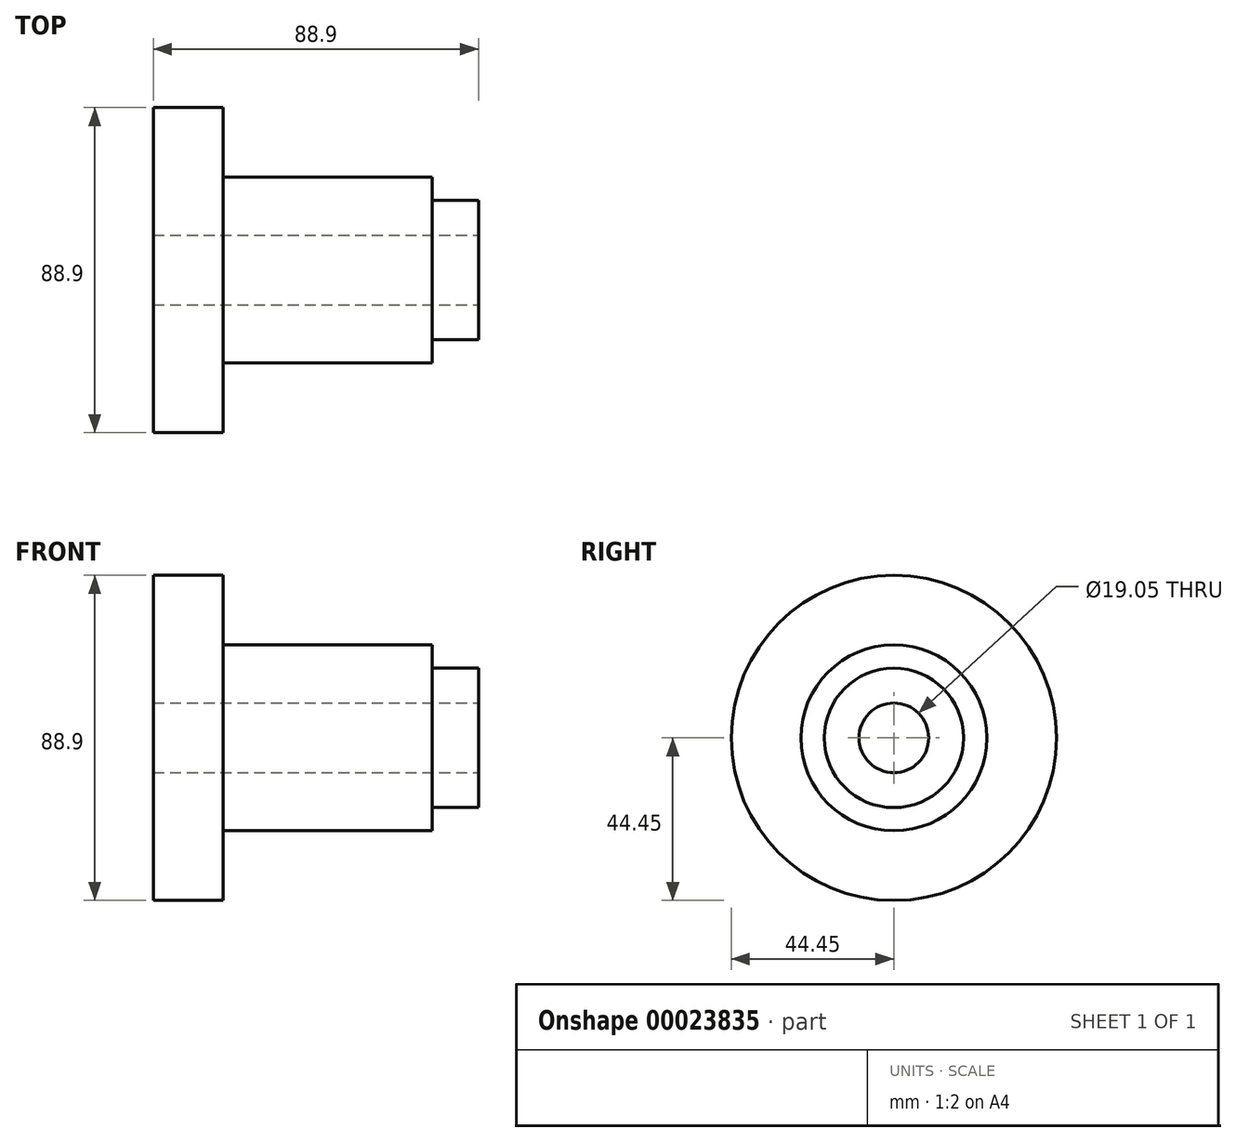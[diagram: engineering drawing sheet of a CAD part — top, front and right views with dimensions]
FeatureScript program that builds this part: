
annotation { "Feature Type Name" : "Feature", "Feature Type Description" : "" }
export const myFeature = defineFeature(function(context is Context, id is Id, definition is map)
    precondition{}
    {
        {
            var Q0;
            Q0=qCreatedBy(makeId("Top.planeOp"),FACE);
            var sketch = newSketch(context, id + "F0", { "sketchPlane" : qUnion([Q0])});
            skLineSegment(sketch, "E0", {"start": v(0, 0) * mm, "end": v(88.4, 0) * mm});
            skLineSegment(sketch, "E1", {"start": v(88.4, 0) * mm, "end": v(-90.15, 0) * mm});
            skLineSegment(sketch, "E2", {"start": v(-62.75, 0) * mm, "end": v(-62.75, 9.52) * mm});
            skLineSegment(sketch, "E3.bottom", {"start": v(-62.75, 9.52) * mm, "end": v(-81.8, 9.52) * mm});
            skLineSegment(sketch, "E3.top", {"start": v(-62.75, 44.45) * mm, "end": v(-81.8, 44.45) * mm});
            skLineSegment(sketch, "E3.left", {"start": v(-62.75, 9.52) * mm, "end": v(-62.75, 44.45) * mm});
            skLineSegment(sketch, "E3.right", {"start": v(-81.8, 9.52) * mm, "end": v(-81.8, 44.45) * mm});
            skLineSegment(sketch, "E4.bottom", {"start": v(-62.75, 9.52) * mm, "end": v(-5.6, 9.52) * mm});
            skLineSegment(sketch, "E4.top", {"start": v(-62.75, 25.4) * mm, "end": v(-5.6, 25.4) * mm});
            skLineSegment(sketch, "E4.left", {"start": v(-62.75, 9.52) * mm, "end": v(-62.75, 25.4) * mm});
            skLineSegment(sketch, "E4.right", {"start": v(-5.6, 9.52) * mm, "end": v(-5.6, 25.4) * mm});
            skLineSegment(sketch, "E5.bottom", {"start": v(-5.6, 9.52) * mm, "end": v(7.1, 9.52) * mm});
            skLineSegment(sketch, "E5.top", {"start": v(-5.6, 19.05) * mm, "end": v(7.1, 19.05) * mm});
            skLineSegment(sketch, "E5.left", {"start": v(-5.6, 9.52) * mm, "end": v(-5.6, 19.05) * mm});
            skLineSegment(sketch, "E5.right", {"start": v(7.1, 9.52) * mm, "end": v(7.1, 19.05) * mm});
            skSolve(sketch);
        }
        {
            var Q0;
            Q0 = qSketchRegion(id + "F0", true);
            var Q1;
            Q1=sQuery(id+"F0.wireOp",EDGE,"E1");
            revolve(context, id + "F1", {"entities" : qUnion([Q0]), "axis" : qUnion([Q1]), "revolveType" : RevolveType.FULL});
        }
    });
